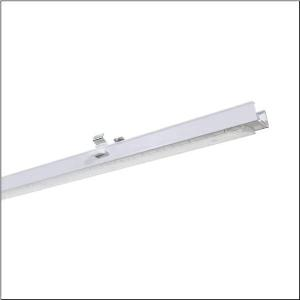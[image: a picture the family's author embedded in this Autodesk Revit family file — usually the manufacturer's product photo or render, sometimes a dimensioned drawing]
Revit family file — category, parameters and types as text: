
# Revit family: trunking_flex_31_51re11db49b
name_source: partatom
category: Lighting Fixtures
units: mm (PartAtom-declared; Revit-internal decimal feet)

## family parameters
Cut with Voids When Loaded = No
Host = Face
Light Source = No
Part Type = Normal
Room Calculation Point = No
Round Connector Dimension = Use Diameter
Shared = No

## types (1)
- --- (1 x LED, 8900 lm, 56 W, 4000K)
    Apparent Load = 56 VA
    CIE Flux Codes = 83 93 98 100 100
    Color Rendering = 80
    Color Temperature = 4000K
    Default Elevation = 1800 mm
    Description = Trunking Flex 31, luminaire insert, of extruded aluminium section, coated, traffic white (RAL 9016), length: 1.472mm, width: 91mm, height: 53mm, LED rated luminous flux: 8.900lm, light colour: 840, control gear: DALI 2, with system connector: socket, mains connection: 220..240V, AC, 50/60Hz, rated input power: 56W, primary light control with lens, of plastic, primary optical cover: cover, of PMMA, light emission: direct distribution, protection rating (complete): IP20, insulation class (complete): insulation class I (protective earthing), certification: CE, UKCA, impact resistance: IK02, permissible ambient temperature for indoor applications: -20..+40°C, packaging unit: 1 piece
    Height = 58 mm
    Lamp = 1 x LED
    Lamp Light Flux = 8900 lm
    Lamp Power = 56 W
    Lamp count = 1
    Length = 1472 mm
    Luminous efficacy = 159 lm/W
    Manufacturer = Siteco
    ModVariant = No
    Model = 51RE11DB49B
    Mounting Place = Ceiling
    Mounting Type = Pendant
    Number of Poles = 1
    OnlyDefault = Yes
    Power Factor = 1
    Product Name = Trunking Flex 31
    Product group = luminaire insert
    ProductGroupID = 901
    Protection Class = Protection class I
    Protection Degree = IP 20
    RLX_Detail_Level = 1
    RLX_Emergency_Light_Flux = 0 lm
    RLX_Emergency_Type = 0
    RLX_Emergency_Type_DB = No
    RlxData = <blob elided: 21693 chars, md5=ba181a4a>
    Socket = socket
    Standby Power = 0 W
    System Light Flux = 8900 lm
    System Power = 56 W
    Type Comments = individual setting: luminous flux: 100 % | (OFF | ON | OFF | OFF) | 1200 mA
    Type Image = l_1266702.jpg
    URL = http://relux.com
    VarID = @adj_018809
    Voltage = 0 V
    Weight = 0.00 kg
    Width = 65 mm

## geometry (parser evidence)
native form markers: Blend x4, Sweep x11
no freeform markers — native parametric forms only
